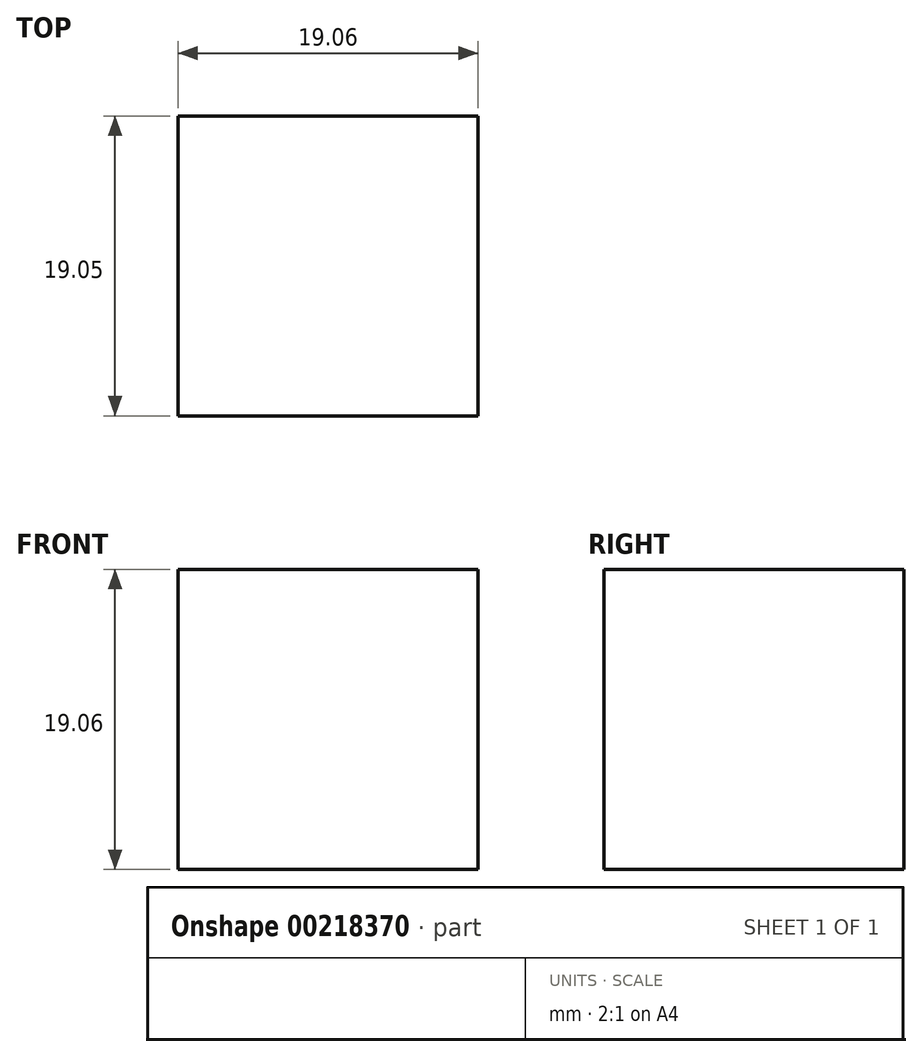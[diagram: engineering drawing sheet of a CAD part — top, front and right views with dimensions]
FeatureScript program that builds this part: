
annotation { "Feature Type Name" : "Feature", "Feature Type Description" : "" }
export const myFeature = defineFeature(function(context is Context, id is Id, definition is map)
    precondition{}
    {
        {
            var Q0;
            Q0=qCreatedBy(makeId("Front.planeOp"),FACE);
            var sketch = newSketch(context, id + "F0", { "sketchPlane" : qUnion([Q0])});
            skLineSegment(sketch, "E0.bottom", {"start": v(-9.52, -9.52) * mm, "end": v(9.53, -9.52) * mm});
            skLineSegment(sketch, "E0.top", {"start": v(-9.53, 9.53) * mm, "end": v(9.52, 9.53) * mm});
            skLineSegment(sketch, "E0.left", {"start": v(-9.52, -9.52) * mm, "end": v(-9.53, 9.53) * mm});
            skLineSegment(sketch, "E0.right", {"start": v(9.53, -9.52) * mm, "end": v(9.52, 9.53) * mm});
            skPoint(sketch, "E0.middle", {"position": v(0, 0) * mm});
            skSolve(sketch);
        }
        {
            var Q0;
            Q0 = qSketchRegion(id + "F0", true);
            extrude(context, id + "F1", {"entities" : qUnion([Q0]), "depth" : 19.05 * mm});
        }
    });
